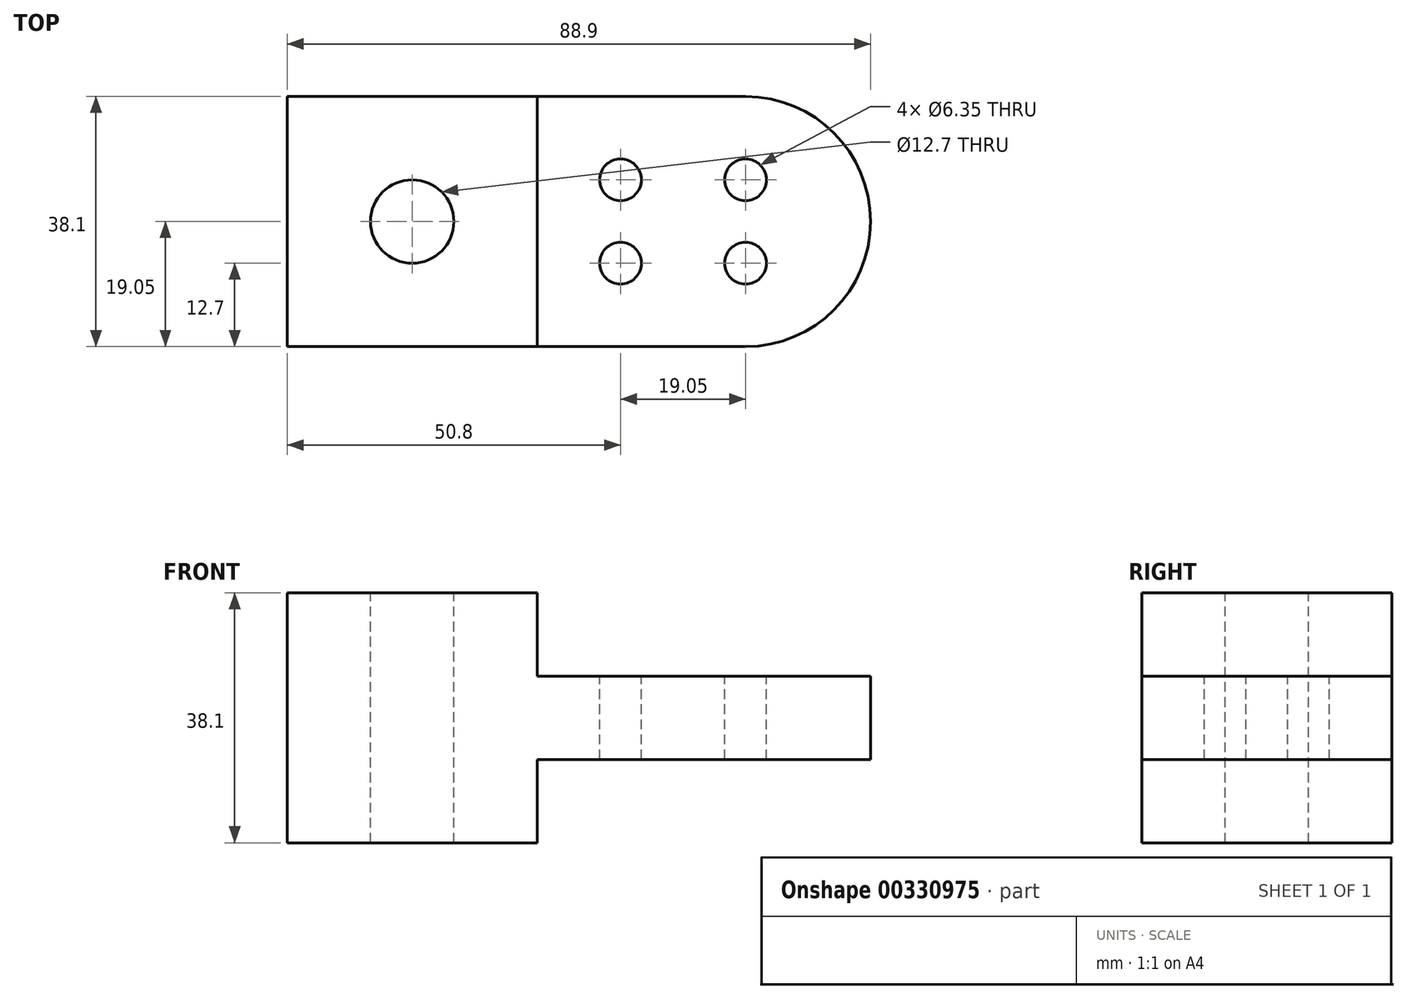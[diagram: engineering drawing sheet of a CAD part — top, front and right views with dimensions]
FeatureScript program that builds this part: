
annotation { "Feature Type Name" : "Feature", "Feature Type Description" : "" }
export const myFeature = defineFeature(function(context is Context, id is Id, definition is map)
    precondition{}
    {
        {
            var Q0;
            Q0=qCreatedBy(makeId("Top.planeOp"),FACE);
            var sketch = newSketch(context, id + "F0", { "sketchPlane" : qUnion([Q0])});
            skLineSegment(sketch, "E0.bottom", {"start": v(0, 0) * mm, "end": v(38.1, 0) * mm});
            skLineSegment(sketch, "E0.top", {"start": v(0, 38.1) * mm, "end": v(38.1, 38.1) * mm});
            skLineSegment(sketch, "E0.left", {"start": v(0, 0) * mm, "end": v(0, 38.1) * mm});
            skLineSegment(sketch, "E0.right", {"start": v(38.1, 0) * mm, "end": v(38.1, 38.1) * mm});
            skSolve(sketch);
        }
        {
            var Q0;
            Q0 = qSketchRegion(id + "F0", true);
            extrude(context, id + "F1", {"entities" : qUnion([Q0]), "endBound" : BoundingType.SYMMETRIC, "depth" : 38.1 * mm});
        }
        {
            var Q0;
            Q0=qCreatedBy(makeId("Top.planeOp"),FACE);
            var sketch = newSketch(context, id + "F2", { "sketchPlane" : qUnion([Q0])});
            skLineSegment(sketch, "E1.bottom", {"start": v(38.1, 0) * mm, "end": v(69.85, 0) * mm});
            skLineSegment(sketch, "E1.top", {"start": v(38.1, 38.1) * mm, "end": v(69.85, 38.1) * mm});
            skLineSegment(sketch, "E1.left", {"start": v(38.1, 0) * mm, "end": v(38.1, 38.1) * mm});
            skLineSegment(sketch, "E1.right", {"start": v(69.85, 0) * mm, "end": v(69.85, 38.1) * mm});
            skSolve(sketch);
        }
        {
            var Q0;
            Q0=makeQuery(id+"F2.imprint","IMPRINT",FACE,{"disambiguationData":[TD([[makeQuery(id+"F2.imprint","IMPRINT",EDGE,{"derivedFrom":sQuery(id+"F2.wireOp",EDGE,"E1.bottom")}),1.0]])]});
            extrude(context, id + "F3", {"entities" : qUnion([Q0]), "operationType" : NewBodyOperationType.ADD, "endBound" : BoundingType.SYMMETRIC, "depth" : 12.7 * mm});
        }
        {
            var Q0;
            Q0=qCreatedBy(makeId("Top.planeOp"),FACE);
            var sketch = newSketch(context, id + "F4", { "sketchPlane" : qUnion([Q0])});
            skArc(sketch, "E2", {"start": v(69.85, 0) * mm, "mid": v(88.9, 19.05) * mm, "end": v(69.85, 38.1) * mm});
            skLineSegment(sketch, "E3", {"start": v(69.85, 38.1) * mm, "end": v(69.85, 0) * mm});
            skSolve(sketch);
        }
        {
            var Q0;
            Q0 = qSketchRegion(id + "F4", true);
            extrude(context, id + "F5", {"entities" : qUnion([Q0]), "operationType" : NewBodyOperationType.ADD, "endBound" : BoundingType.SYMMETRIC, "depth" : 12.7 * mm});
        }
        {
            var Q0;
            Q0=makeQuery(id+"F1.opExtrude","CAP_FACE",FACE,{"disambiguationData":[OSD([sQuery(id+"F0.wireOp",EDGE,"E0.bottom"),sQuery(id+"F0.wireOp",EDGE,"E0.top"),sQuery(id+"F0.wireOp",EDGE,"E0.left"),sQuery(id+"F0.wireOp",EDGE,"E0.right")])],"isStart":false});
            var sketch = newSketch(context, id + "F6", { "sketchPlane" : qUnion([Q0])});
            skCircle(sketch, "E4", {"center": v(19.05, 19.05) * mm, "radius": 6.35 * mm});
            skPoint(sketch, "E4.centerSnap0", {"position": v(0, 19.05) * mm});
            skPoint(sketch, "E4.centerSnap1", {"position": v(19.05, 0) * mm});
            skSolve(sketch);
        }
        {
            var Q0;
            Q0 = qSketchRegion(id + "F6", true);
            extrude(context, id + "F7", {"entities" : qUnion([Q0]), "operationType" : NewBodyOperationType.REMOVE, "endBound" : BoundingType.THROUGH_ALL, "oppositeDirection" : true, "depth" : 25.4 * mm});
        }
        {
            var Q0;
            Q0=makeQuery(id+"F5.boolean.opBoolean","MERGE",FACE,{"derivedFrom":[makeQuery(id+"F3.opExtrude","CAP_FACE",FACE,{"disambiguationData":[OSD([sQuery(id+"F2.wireOp",EDGE,"E1.bottom"),sQuery(id+"F2.wireOp",EDGE,"E1.top"),sQuery(id+"F2.wireOp",EDGE,"E1.left"),sQuery(id+"F2.wireOp",EDGE,"E1.right")])],"isStart":false}),makeQuery(id+"F5.opExtrude","CAP_FACE",FACE,{"disambiguationData":[OSD([sQuery(id+"F4.wireOp",EDGE,"E2"),sQuery(id+"F4.wireOp",EDGE,"E3")])],"isStart":false})]});
            var sketch = newSketch(context, id + "F8", { "sketchPlane" : qUnion([Q0])});
            skCircle(sketch, "E5", {"center": v(69.85, 25.4) * mm, "radius": 3.18 * mm});
            skCircle(sketch, "E6", {"center": v(69.85, 12.7) * mm, "radius": 3.18 * mm});
            skCircle(sketch, "E7", {"center": v(50.8, 25.4) * mm, "radius": 3.18 * mm});
            skCircle(sketch, "E8", {"center": v(50.8, 12.7) * mm, "radius": 3.18 * mm});
            skSolve(sketch);
        }
        {
            var Q0;
            Q0 = qSketchRegion(id + "F8", true);
            extrude(context, id + "F9", {"entities" : qUnion([Q0]), "operationType" : NewBodyOperationType.REMOVE, "endBound" : BoundingType.THROUGH_ALL, "oppositeDirection" : true, "depth" : 25.4 * mm});
        }
    });
